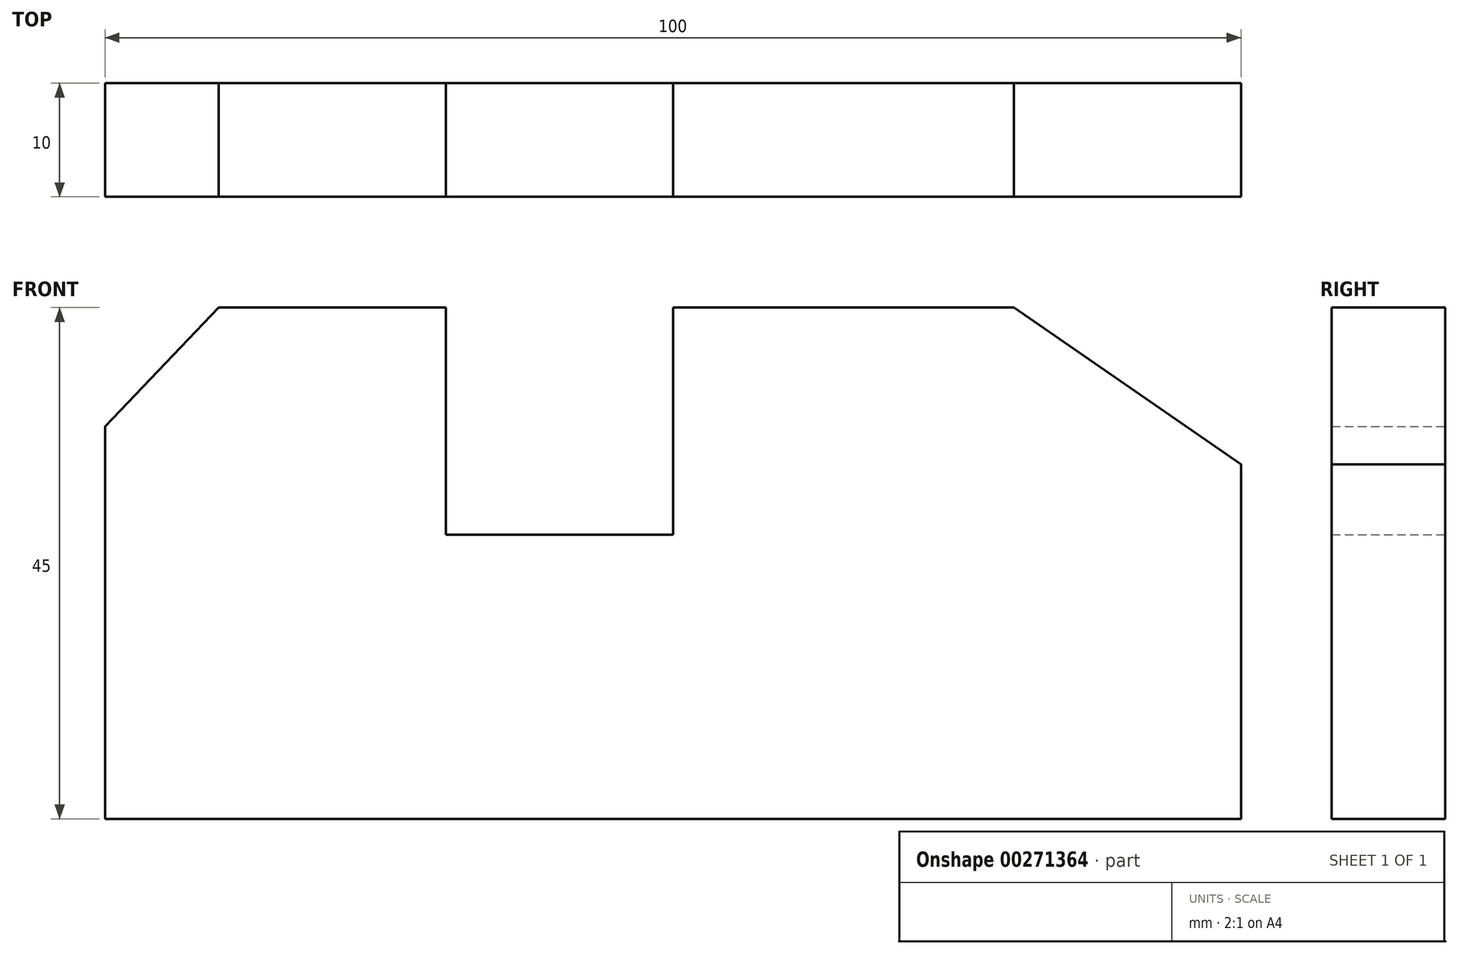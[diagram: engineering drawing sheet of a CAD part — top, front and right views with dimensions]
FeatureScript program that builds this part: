
annotation { "Feature Type Name" : "Feature", "Feature Type Description" : "" }
export const myFeature = defineFeature(function(context is Context, id is Id, definition is map)
    precondition{}
    {
        {
            var Q0;
            Q0=qCreatedBy(makeId("Front.planeOp"),FACE);
            var sketch = newSketch(context, id + "F0", { "sketchPlane" : qUnion([Q0])});
            skLineSegment(sketch, "E0.bottom", {"start": v(0, 0) * mm, "end": v(100, 0) * mm});
            skLineSegment(sketch, "E0.top", {"start": v(10, 45) * mm, "end": v(30, 45) * mm});
            skLineSegment(sketch, "E0.left", {"start": v(0, 0) * mm, "end": v(0, 34.54) * mm});
            skLineSegment(sketch, "E0.right", {"start": v(100, 0) * mm, "end": v(100, 31.2) * mm});
            skPoint(sketch, "E1", {"position": v(30, 45) * mm});
            skPoint(sketch, "E2", {"position": v(10, 45) * mm});
            skLineSegment(sketch, "E3", {"start": v(10, 45) * mm, "end": v(0, 34.54) * mm});
            skPoint(sketch, "E4", {"position": v(30, 25) * mm});
            skLineSegment(sketch, "E5", {"start": v(30, 45) * mm, "end": v(30, 25) * mm});
            skLineSegment(sketch, "E6", {"start": v(30, 25) * mm, "end": v(50, 25) * mm});
            skLineSegment(sketch, "E7", {"start": v(50, 25) * mm, "end": v(50, 45) * mm});
            skLineSegment(sketch, "E8.trimOffspring", {"start": v(50, 45) * mm, "end": v(80, 45) * mm});
            skPoint(sketch, "E9", {"position": v(80, 45) * mm});
            skLineSegment(sketch, "E10", {"start": v(80, 45) * mm, "end": v(100, 31.2) * mm});
            skSolve(sketch);
        }
        {
            var Q0;
            Q0 = qSketchRegion(id + "F0", true);
            extrude(context, id + "F1", {"entities" : qUnion([Q0]), "depth" : 10 * mm});
        }
    });
